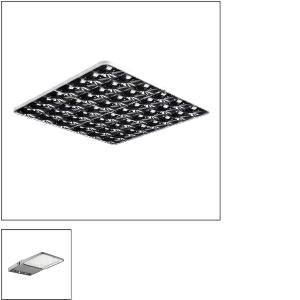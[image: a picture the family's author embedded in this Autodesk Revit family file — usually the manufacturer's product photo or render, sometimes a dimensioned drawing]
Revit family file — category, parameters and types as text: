
# Revit family: siteco_mirrortec_r__indoor___rs05_5nw14093qb_2604
name_source: partatom
category: Lighting Fixtures
units: mm (PartAtom-declared; Revit-internal decimal feet)

## family parameters
Cut with Voids When Loaded = No
Host = Face
Light Source = No
Part Type = Normal
Room Calculation Point = No
Round Connector Dimension = Use Diameter
Shared = No

## types (1)
- 5XA7682G2H2AC (1 x LED, 33820 lm, 305.7 W, 4000K)
    Apparent Load = 306 VA
    CIE Flux Codes = 47 83 98 55 100
    Color Rendering = 70
    Color Temperature = 4000K
    Default Elevation = 1800 mm
    Description = secondary reflector, for Siteco Mirrortec® Indoor, wire hanger, housing, square, of aluminium, coated, metallic grey (RAL 9006), fresnel reflector 100, of PMMA, aluminized, highly specular, light point resolution, fresnel structure, length: 900 mm, width: 900 mm

Light Distribution: RS05
    Height = 12 mm  [stored 0.0393701 ft]
    Lamp = 1 x LED
    Lamp Light Flux = 33820 lm
    Lamp Power = 305.7 W
    Lamp count = 1
    Length = 919 mm
    Luminous efficacy = 111 lm/W
    Manufacturer = Siteco
    ModVariant = No
    Model = 5NW14093QB
    Mounting Place = Ceiling
    Mounting Type = Pendant
    Number of Poles = 1
    OnlyDefault = Yes
    Power Factor = 1
    Product Name = Siteco Mirrortec® Indoor | RS05
    Product group = secondary reflector
    ProductGroupID = 908
    Protection Class = Protection class II
    Protection Degree = IP 66
    RLX_Detail_Level = 1
    RLX_Emergency_Light_Flux = 0 lm
    RLX_Emergency_Type = 0
    RLX_Emergency_Type_DB = No
    RlxData = <blob elided: 103317 chars, md5=b65ad5a1>
    Socket = socket
    Standby Power = 0 W
    System Light Flux = 33820 lm
    System Power = 306 W
    Type Comments = Floodlight FL 20 midi, floodlight, primary light control with lens, of plastic, primary optical cover: protective disc, of toughened safety glass, transparent, light distribution: RS05, light emission: direct distribution, primary light characteristic: rotationally symmetric, installation type: surface-mounted, LED, High Power LED, rated luminous flux: 38.380lm, luminous efficacy: 126lm/W, light colour: 740, colour temperature: 4000K, control gear: ECG Plus, control: overheat protection, power reduction, digital communication interface, time-dependent luminous flux control, flexible luminous flux parameterisation, electronic power reduction, with terminal, 10-pole, max. 2.5mm², mains connection: 220..240V, AC, 50/60Hz, rated input power: 306W, LED unit, of diecast aluminium, powder-coated, Siteco® metallic grey (DB 702S), corrosivity category C5 mid according to DIN EN ISO 12944, length: 731mm, width: 450mm, height: 76mm, housing frame, of diecast aluminium, powder-coated, Siteco® metallic grey (DB 702S), wall fastening, DALI, protection rating (complete): IP66, insulation class (complete): insulation class II (safety insulation), certification: CE, ENEC, VDE, protection symbol: D, permissible operating ambient temperature: -40..+40°C, permissible operating ambient temperature for outdoor applications: -40..+50°C, standard: DIN EN 12944, packaging unit: 1 piece

individual setting: distance floodlight mirror = 2,5m / reflector tilt = 5°
    Type Image = l_577132_1005944.jpg
    URL = http://relux.com
    VarID = 5xa7682g2h2ac@adj_135713
    Voltage = 0 V
    Weight = 0.00 kg
    Width = 919 mm

note: [stored X ft] marks values corroborated as IEEE doubles in the binary element streams (Revit-internal decimal feet)

## geometry (parser evidence)
native form markers: Blend x4, Sweep x9
no freeform markers — native parametric forms only
